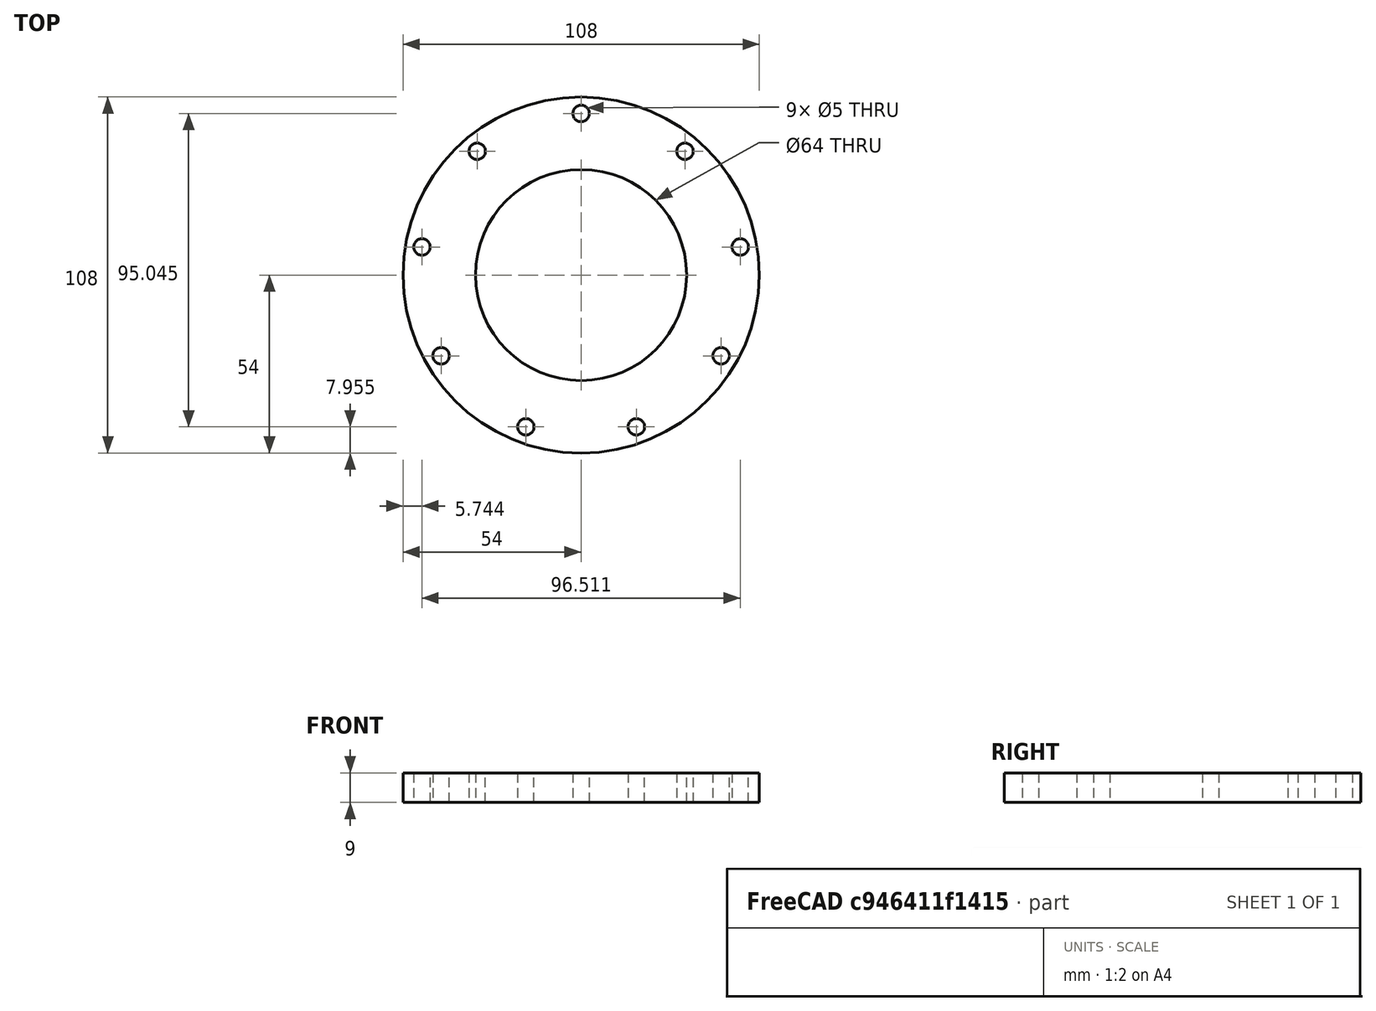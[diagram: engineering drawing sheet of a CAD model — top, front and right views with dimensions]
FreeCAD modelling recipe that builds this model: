
FCSTD DOCUMENT  (FreeCAD 0.19R24276 (Git))
Label: BLDC_GT2_part_1_d75_d128_v3_for_disk_bolgarki
License: All rights reserved
LicenseURL: http://en.wikipedia.org/wiki/All_rights_reserved
objects: Sketcher::SketchObject×1, PartDesign::Pad×1, PartDesign::Body×1
note: 4 computed .brp shape members not serialized (recipe doc carries the construction recipe); baked Part::Feature solids carry a one-line shape summary decoded from their .brp

FEATURE [Sketcher::SketchObject] Sketch  label="Sketch_d64_d108x9otvxd5_d98"
  FullyConstrained = true
  MapMode = 5
  Support = -> [XY_Plane]
  sketch-geometry (21):
    g0: Circle CenterX=0 CenterY=0 CenterZ=0 NormalX=0 NormalY=0 NormalZ=1 AngleXU=0 Radius=54
    g1: Circle CenterX=0 CenterY=0 CenterZ=0 NormalX=0 NormalY=0 NormalZ=1 AngleXU=0 Radius=32
    g2: LineSegment StartX=0 StartY=49 StartZ=0 EndX=-31.4966 EndY=37.5362 EndZ=0
    g3: LineSegment StartX=-31.4966 StartY=37.5362 StartZ=0 EndX=-48.2556 EndY=8.50876 EndZ=0
    g4: LineSegment StartX=-48.2556 StartY=8.50876 StartZ=0 EndX=-42.4352 EndY=-24.5 EndZ=0
    g5: LineSegment StartX=-42.4352 StartY=-24.5 StartZ=0 EndX=-16.759 EndY=-46.0449 EndZ=0
    g6: LineSegment StartX=-16.759 StartY=-46.0449 StartZ=0 EndX=16.759 EndY=-46.0449 EndZ=0
    g7: LineSegment StartX=16.759 StartY=-46.0449 StartZ=0 EndX=42.4352 EndY=-24.5 EndZ=0
    g8: LineSegment StartX=42.4352 StartY=-24.5 StartZ=0 EndX=48.2556 EndY=8.50876 EndZ=0
    g9: LineSegment StartX=48.2556 StartY=8.50876 StartZ=0 EndX=31.4966 EndY=37.5362 EndZ=0
    g10: LineSegment StartX=31.4966 StartY=37.5362 StartZ=0 EndX=0 EndY=49 EndZ=0
    g11: Circle CenterX=0 CenterY=0 CenterZ=0 NormalX=0 NormalY=0 NormalZ=1 AngleXU=0 Radius=49
    g12: Circle CenterX=31.4966 CenterY=37.5362 CenterZ=0 NormalX=0 NormalY=0 NormalZ=1 AngleXU=0 Radius=2.5
    g13: Circle CenterX=48.2556 CenterY=8.50876 CenterZ=0 NormalX=0 NormalY=0 NormalZ=1 AngleXU=0 Radius=2.5
    g14: Circle CenterX=42.4352 CenterY=-24.5 CenterZ=0 NormalX=0 NormalY=0 NormalZ=1 AngleXU=0 Radius=2.5
    g15: Circle CenterX=16.759 CenterY=-46.0449 CenterZ=0 NormalX=0 NormalY=0 NormalZ=1 AngleXU=0 Radius=2.5
    g16: Circle CenterX=-16.759 CenterY=-46.0449 CenterZ=0 NormalX=0 NormalY=0 NormalZ=1 AngleXU=0 Radius=2.5
    g17: Circle CenterX=-42.4352 CenterY=-24.5 CenterZ=0 NormalX=0 NormalY=0 NormalZ=1 AngleXU=0 Radius=2.5
    g18: Circle CenterX=-48.2556 CenterY=8.50876 CenterZ=0 NormalX=0 NormalY=0 NormalZ=1 AngleXU=0 Radius=2.5
    g19: Circle CenterX=-31.4966 CenterY=37.5362 CenterZ=0 NormalX=0 NormalY=0 NormalZ=1 AngleXU=0 Radius=2.5
    g20: Circle CenterX=0 CenterY=49 CenterZ=0 NormalX=0 NormalY=0 NormalZ=1 AngleXU=0 Radius=2.5
  constraints (37):
    c: Coincident(g0,g-1)
    c: Diameter(g0) = 108
    c: Coincident(g1,g0)
    c: Diameter(g1) = 64
    c: Coincident(g2,g3)
    c: Coincident(g3,g4)
    c: Coincident(g4,g5)
    c: Coincident(g5,g6)
    c: Coincident(g6,g7)
    c: Coincident(g7,g8)
    c: Coincident(g8,g9)
    c: Coincident(g9,g10)
    c: Coincident(g10,g2)
    c: Equal(g2, g3-g10) x8
    c: PointOnObject(g2,g11)
    c: PointOnObject(g3,g11)
    c: PointOnObject(g4,g11)
    c: PointOnObject(g5,g11)
    c: PointOnObject(g6,g11)
    c: PointOnObject(g7,g11)
    c: PointOnObject(g8,g11)
    c: PointOnObject(g9,g11)
    c: PointOnObject(g10,g11)
    c: Coincident(g11,g0)
    c: Diameter(g11) = 98
    c: Coincident(g12,g9)
    c: Coincident(g13,g8)
    c: Coincident(g14,g7)
    c: Coincident(g15,g6)
    c: Coincident(g16,g5)
    c: Coincident(g17,g4)
    c: Coincident(g18,g3)
    c: Coincident(g19,g2)
    c: Coincident(g20,g2)
    c: Vertical(g20,g0)
    c: Diameter(g20) = 5
    c: Equal(g20, g12-g19) x8
FEATURE [PartDesign::Pad] Pad  label="Pad_h9"
  Direction = (1,1,1)
  Length = 9
  Length2 = 100
  Profile = -> Sketch
  Type = 0
FEATURE [PartDesign::Body] Body
  Group = -> [Sketch,Pad]
  Origin = -> Origin
  Tip = -> Pad
